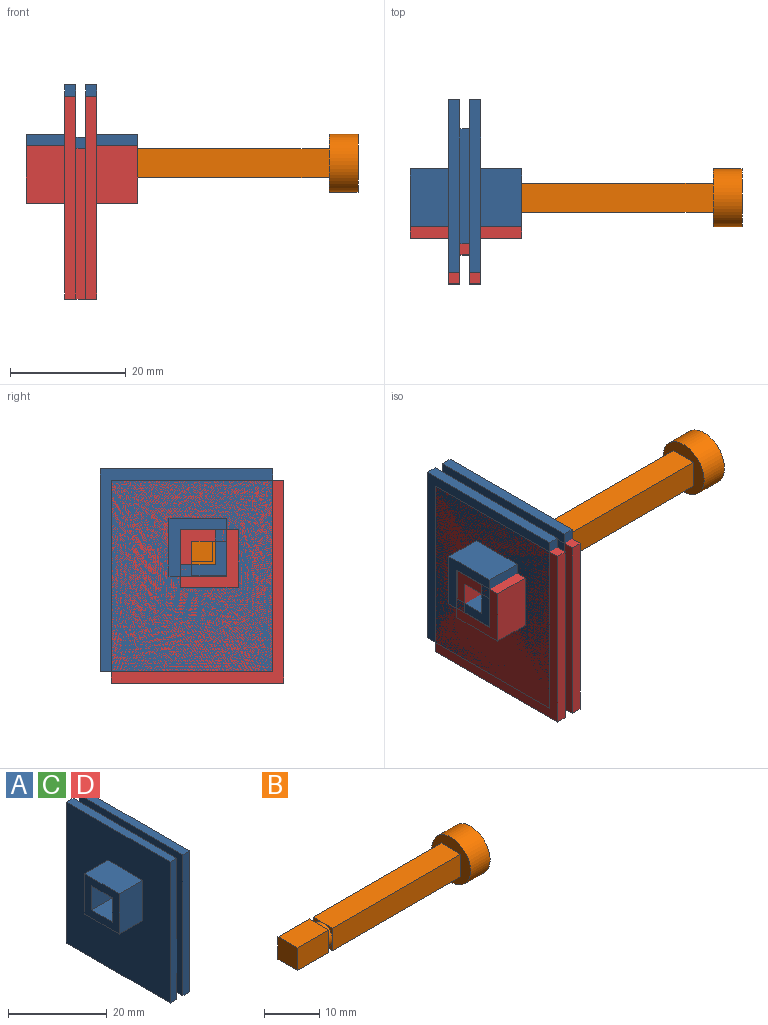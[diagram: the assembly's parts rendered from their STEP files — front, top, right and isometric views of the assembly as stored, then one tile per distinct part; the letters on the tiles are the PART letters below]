
ASSEMBLY  parts=4 mates=1
PART A: 28 faces, bbox 19.3x29.8x35 mm
  f0: plane 29.8x1.9mm, normal (0,0,1), area 56.6mm2, adj f2,f3,f4,f10
  f1: plane 35x29.8mm, normal (-1,0,0), area 943mm2, adj f5,f6,f7,f8,f18,f19,f20,f21
  f2: plane 35x29.8mm, normal (1,0,0), area 943mm2, adj f0,f3,f4,f6,f14,f15,f16,f17
  f3: plane 35x1.9mm, normal (0,-1,0), area 66.5mm2, adj f0,f2,f6,f10
  f4: plane 35x1.9mm, normal (0,1,0), area 66.5mm2, adj f0,f2,f6,f10
  f5: plane 29.8x1.9mm, normal (0,0,1), area 56.6mm2, adj f1,f7,f8,f11
  f6: plane 29.8x5.5mm, normal (0,0,-1), area 146.9mm2, adj f1,f2,f3,f4,f7,f8,f9,f10
  f7: plane 35x1.9mm, normal (0,-1,0), area 66.5mm2, adj f1,f5,f6,f11
  f8: plane 35x1.9mm, normal (0,1,0), area 66.5mm2, adj f1,f5,f6,f11
  f9: plane 26x1.7mm, normal (0,-1,0), area 44.2mm2, adj f6,f10,f11,f27
  f10: plane 35x29.8mm, normal (-1,0,0), area 528.2mm2, adj f0,f3,f4,f6,f9,f12,f27
  f11: plane 35x29.8mm, normal (1,0,0), area 528.2mm2, adj f5,f6,f7,f8,f9,f12,f27
  f12: plane 26x1.7mm, normal (0,1,0), area 44.2mm2, adj f6,f10,f11,f27
  f13: plane 10x10mm, normal (1,0,0), area 64mm2, adj f14,f15,f16,f17,f23,f24,f25,f26
  f14: plane 10x7.1mm, normal (0,0,1), area 71mm2, adj f2,f13,f15,f17
  f15: plane 10x7.1mm, normal (0,1,0), area 71mm2, adj f2,f13,f14,f16
  f16: plane 10x7.1mm, normal (0,0,-1), area 71mm2, adj f2,f13,f15,f17
  f17: plane 10x7.1mm, normal (0,-1,0), area 71mm2, adj f2,f13,f14,f16
  f18: plane 10x6.7mm, normal (0,-1,0), area 67mm2, adj f1,f19,f21,f22
  f19: plane 10x6.7mm, normal (0,0,-1), area 67mm2, adj f1,f18,f20,f22
  f20: plane 10x6.7mm, normal (0,1,0), area 67mm2, adj f1,f19,f21,f22
  f21: plane 10x6.7mm, normal (0,0,1), area 67mm2, adj f1,f18,f20,f22
  f22: plane 10x10mm, normal (-1,0,0), area 64mm2, adj f18,f19,f20,f21,f23,f24,f25,f26
  f23: plane 19.3x6mm, normal (0,-1,0), area 115.8mm2, adj f13,f22,f24,f26
  f24: plane 19.3x6mm, normal (0,0,1), area 115.8mm2, adj f13,f22,f23,f25
  f25: plane 19.3x6mm, normal (0,1,0), area 115.8mm2, adj f13,f22,f24,f26
  f26: plane 19.3x6mm, normal (0,0,-1), area 115.8mm2, adj f13,f22,f23,f25
  f27: plane 19.8x1.7mm, normal (0,0,1), area 33.7mm2, adj f9,f10,f11,f12
PART B: 21 faces, bbox 47x10x10 mm
  f0: plane 0.5x0.01mm, normal (-1,0,0), area 0mm2, adj f12,f18
  f1: plane 2.5x2.5mm, normal (-1,0,0), area 1.3mm2, adj f4,f5,f12
  f2: plane 2.5x2.5mm, normal (-1,0,0), area 1.3mm2, adj f4,f7,f12
  f3: plane 2.5x2.5mm, normal (-1,0,0), area 1.3mm2, adj f6,f7,f12
  f4: plane 33x5mm, normal (0,0,1), area 165mm2, adj f1,f2,f5,f7,f11
  f5: plane 33x5mm, normal (0,-1,0), area 165mm2, adj f1,f4,f6,f8,f11
  f6: plane 33x5mm, normal (0,0,-1), area 165mm2, adj f3,f5,f7,f8,f11
  f7: plane 33x5mm, normal (0,1,0), area 165mm2, adj f2,f3,f4,f6,f11
  f8: plane 2.5x2.5mm, normal (-1,0,0), area 1.3mm2, adj f5,f6,f12
  f9: cylinder r=5mm len=10mm, axis (-1,0,0), area 157.1mm2, adj f10,f11
  f10: plane 10x10mm, normal (1,0,0), area 78.5mm2, adj f9
  f11: plane 10x10mm, normal (-1,0,0), area 53.5mm2, adj f4,f5,f6,f7,f9
  f12: cylinder r=2.5mm len=5mm, axis (1,0,0), area 15.7mm2, adj f0,f1,f2,f3,f8,f13,f14,f15
  f13: plane 1.43x0.1mm, normal (-1,0,0), area 0.1mm2, adj f12,f17
  f14: plane 5x5mm, normal (1,0,0), area 4.4mm2, adj f12,f16,f17,f18,f19
  f15: plane 2.15x1.77mm, normal (1,0,0), area 1.1mm2, adj f12,f17,f18
  f16: plane 8x5mm, normal (0,1,0), area 40mm2, adj f14,f17,f19,f20
  f17: plane 8x5mm, normal (0,0,-1), area 40mm2, adj f13,f14,f15,f16,f18,f20
  f18: plane 8x5mm, normal (0,-1,0), area 40mm2, adj f0,f14,f15,f17,f19,f20
  f19: plane 8x5mm, normal (0,0,1), area 40mm2, adj f14,f16,f18,f20
  f20: plane 5x5mm, normal (-1,0,0), area 25mm2, adj f16,f17,f18,f19
PART C: same geometry as A
PART D: same geometry as A
PLACE A t=(-13.85,1.88,-2.21)mm
PLACE B t=(-8.34,-2.19,19.29)mm
PLACE C t=(-13.85,1.88,-2.21)mm
PLACE D t=(-13.85,-0.06,-4.16)mm
MATE slider B.f8 <-> D.f13  axis (-1,0,0) through (-8.34,-4.14,17.34)mm
